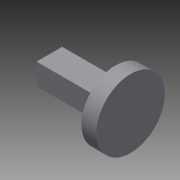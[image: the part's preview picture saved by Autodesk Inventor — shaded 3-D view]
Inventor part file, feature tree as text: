
AUTODESK INVENTOR PART (.ipt)
format: ipt  version: 2015 (Build 190159000, 159)  size: 90,624 bytes
history: native  units: in
note: dims shown in document units (in); Inventor stores cm internally (conversion verified against a paired STEP export)
features: extrude x3, sketch x3
ambient origin geometry x8: Origin, YZ Plane, XZ Plane, XY Plane, X Axis, Y Axis, Z Axis, Center Point
bodies: Solid1 (feature_tree)
feature tree (6):
  extrude  "Extrusion1"  Depth=0.2362in
  extrude  "Extrusion2"  Depth=1.0236in
  extrude  "Extrusion3"  Depth=0.2756in
  sketch  "Sketch1"  dims[d0=0.2362in d1=0.2362in]
  sketch  "Sketch2"  dims[d2=1.0236in d3=0.5118in]
  sketch  "Sketch3"  dims[d4=0.3937in d5=0.0in d6=0.0787in d7=0.1969in d8=0.0in d9=1.2598in d10=0.2756in d11=0.0in]
